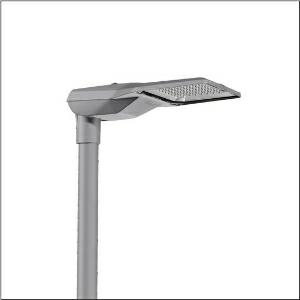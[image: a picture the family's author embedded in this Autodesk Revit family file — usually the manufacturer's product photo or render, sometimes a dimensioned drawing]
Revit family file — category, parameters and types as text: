
# Revit family: streetlight_sl_21_midi___st1_5a_5xe3p33s08lb_eae5
name_source: partatom
category: Lighting Fixtures
units: mm (PartAtom-declared; Revit-internal decimal feet)

## family parameters
Cut with Voids When Loaded = No
Host = Face
Light Source = No
Part Type = Normal
Room Calculation Point = No
Round Connector Dimension = Use Diameter
Shared = No

## types (1)
- --- (1 x LED, 14100 lm, 99.6 W, 3000K)
    Apparent Load = 100 VA
    CIE Flux Codes = 22 53 95 100 100
    Color Rendering = 70
    Color Temperature = 3000K
    Default Elevation = 1800 mm
    Description = Streetlight SL 21 midi, mast luminaire, primary light control with lens, of PMMA, primary optical cover: cover, of toughened safety glass, transparent, light distribution: ST1.5a, light emission: direct distribution, primary light characteristic: asymmetric, installation type: side-entry, post-top, LED, High Power LED, rated luminous flux: 14.100lm, luminous efficacy: 142lm/W, light colour: 730, colour temperature: 3000K, control gear: D4i, control: overheat protection, constant luminous flux control, time-dependent luminous flux control, flexible luminous flux parameterisation, pre-setting: logarithmic dimming characteristic, mains connection: 230..240V, AC, 50/60Hz, start of lifetime: 100W, end of service life: 102W, reduction: 46W, luminaire housing, of diecast aluminium, powder-coated, SITECO metallic grey (DB 702S), corrosivity category C5 high according to DIN EN ISO 12944, please order mast flange separately, inclination adjustable: 0°, 5°, 10°, 15°, sealing non-destructively replaceable, multi-level sealing system, length: 644mm, width: 335mm, height: 110mm, mast flange for spigot size: 42mm (side-entry): 5XC10008XM4, 60/48mm (side-entry/post-top): 5XC10108XM2, 76/60mm (side-entry/post-top): 5XC10108XM1, mounting height: 4..8m, Smart Interface above, protection rating (complete): IP66, insulation class (complete): insulation class II (safety insulation), certification: CE, ENEC, ENEC+, VDE, impact resistance: IK10, permissible operating ambient temperature for outdoor applications: -40..+50°C, standard-compliant lighting for roads and squares, packaging unit: 1 piece

Light Distribution: ST1.5a
    Height = 111 mm
    Lamp = 1 x LED
    Lamp Light Flux = 14100 lm
    Lamp Power = 99.6 W
    Lamp count = 1
    Length = 644 mm
    Luminous efficacy = 142 lm/W
    Manufacturer = Siteco
    ModVariant = No
    Model = 5XE3P33S08LB
    Number of Poles = 1
    OnlyDefault = Yes
    Power Factor = 1
    Product Name = Streetlight SL 21 midi | ST1.5a
    Product group = mast luminaire | pylon top
    ProductGroupID = 6100
    Protection Class = Protection class II
    Protection Degree = IP 66
    RLX_Detail_Level = 1
    RLX_Emergency_Light_Flux = 0 lm
    RLX_Emergency_Type = 0
    RLX_Emergency_Type_DB = No
    RlxData = <blob elided: 30321 chars, md5=b4475e09>
    Socket = socket
    Standby Power = 0 W
    System Light Flux = 14100 lm
    System Power = 100 W
    Type Comments = factory setting: luminous flux: 100 % | dim-lin: 254 | 1020 mA
    Type Image = l_1004302.jpg
    URL = http://relux.com
    VarID = @adj_032529
    Voltage = 0 V
    Weight = 0.00 kg
    Width = 336 mm

## geometry (parser evidence)
native form markers: Blend x4, Sweep x10
no freeform markers — native parametric forms only
